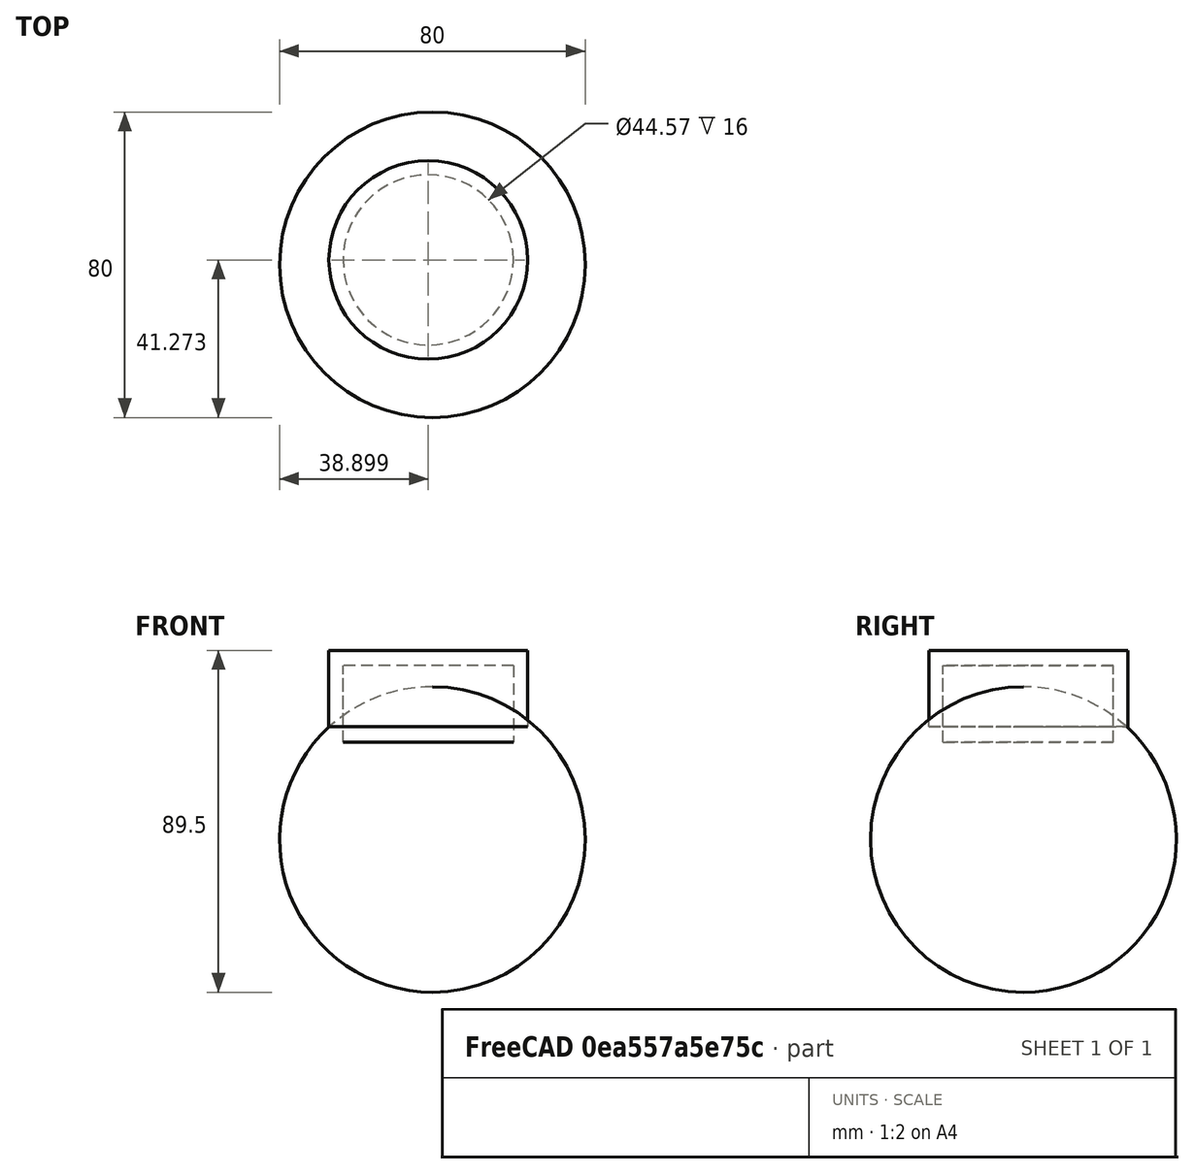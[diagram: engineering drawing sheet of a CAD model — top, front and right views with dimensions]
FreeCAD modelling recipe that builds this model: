
FCSTD DOCUMENT  (FreeCAD 1.1R20260325 (Git shallow))
Label: Conj_iluminacao_Spot_Laje
License: All rights reserved
LicenseURL: http://en.wikipedia.org/wiki/All_rights_reserved
objects: Part::FeaturePython×1, Part::Feature×1, App::DocumentObjectGroup×1
note: 2 computed .brp shape members not serialized (recipe doc carries the construction recipe); baked Part::Feature solids carry a one-line shape summary decoded from their .brp

FEATURE [Part::FeaturePython] Component  label="Caixa Passagem Embutir Spot Laje"  # Arch/BIM 0 (typed FeaturePython)
  HorizontalArea = 0
  IfcData = attributes={"GlobalId": {"name": "GlobalId", "type": "IfcGloballyUniqueId", "is_enum": false, "enum_values": []}, "Description": {"... (+538 chars omitted),+1 more (map truncated)
  IfcType = 0
  MoveBase = false
  MoveWithHost = false
  PerimeterLength = 0
  Placement = pos=(-206.23,283.21,3000) rot=(0,0,1;0rad)
  PredefinedType = 0
  VerticalArea = 0
FEATURE [Part::Feature] Compound002002002004005002002003003002003005002002005002002002001  label="Bocal e Lampada"
  Base_StandardCode = 23-35 47 11
  Placement = pos=(261.62,1616.83,3018) rot=(1,0,0;3.14159rad)
  shape: bbox 150 x 168 x 98.5 mm, 18 faces, 5 solids (baked)
FEATURE [App::DocumentObjectGroup] Group  label="Conj_iluminacao_spot_laje"
  Group = -> [Component,Compound002002002004005002002003003002003005002002005002002002001]
